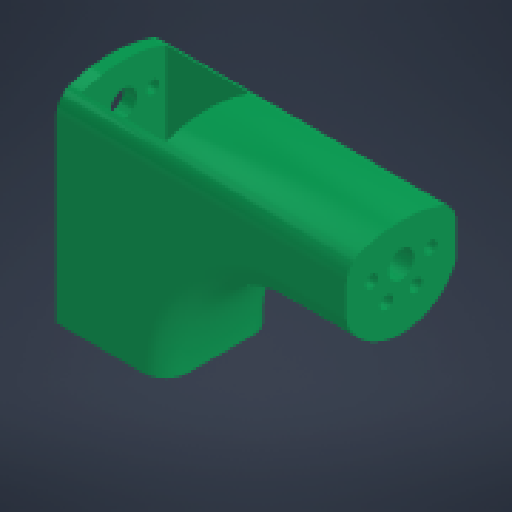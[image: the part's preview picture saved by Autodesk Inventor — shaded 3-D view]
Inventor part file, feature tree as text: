
AUTODESK INVENTOR PART (.ipt)
format: ipt  version: 2024 (Build 280153000, 153)  size: 288,768 bytes
history: native  units: mm
features: other x3, extrude x2, sketch x2, imported_body x1, fillet x1
ambient origin geometry x8: Origin, YZ Plane, XZ Plane, XY Plane, X Axis, Y Axis, Z Axis, Center Point
bodies: Body1 (feature_tree)
feature tree (9):
  other  "Твердое тело1"
  imported_body  "БазТело1"
  extrude  "Выдавливание1"  Depth=14.0mm
  extrude  "Выдавливание2"  Depth=3.0mm
  other  "Непосредственное редактирование2"
  fillet  "Сопряжение2"  Radius=9.0mm
  sketch  "Эскиз2"
  sketch  "Эскиз3"
  other  "Перенос2"
